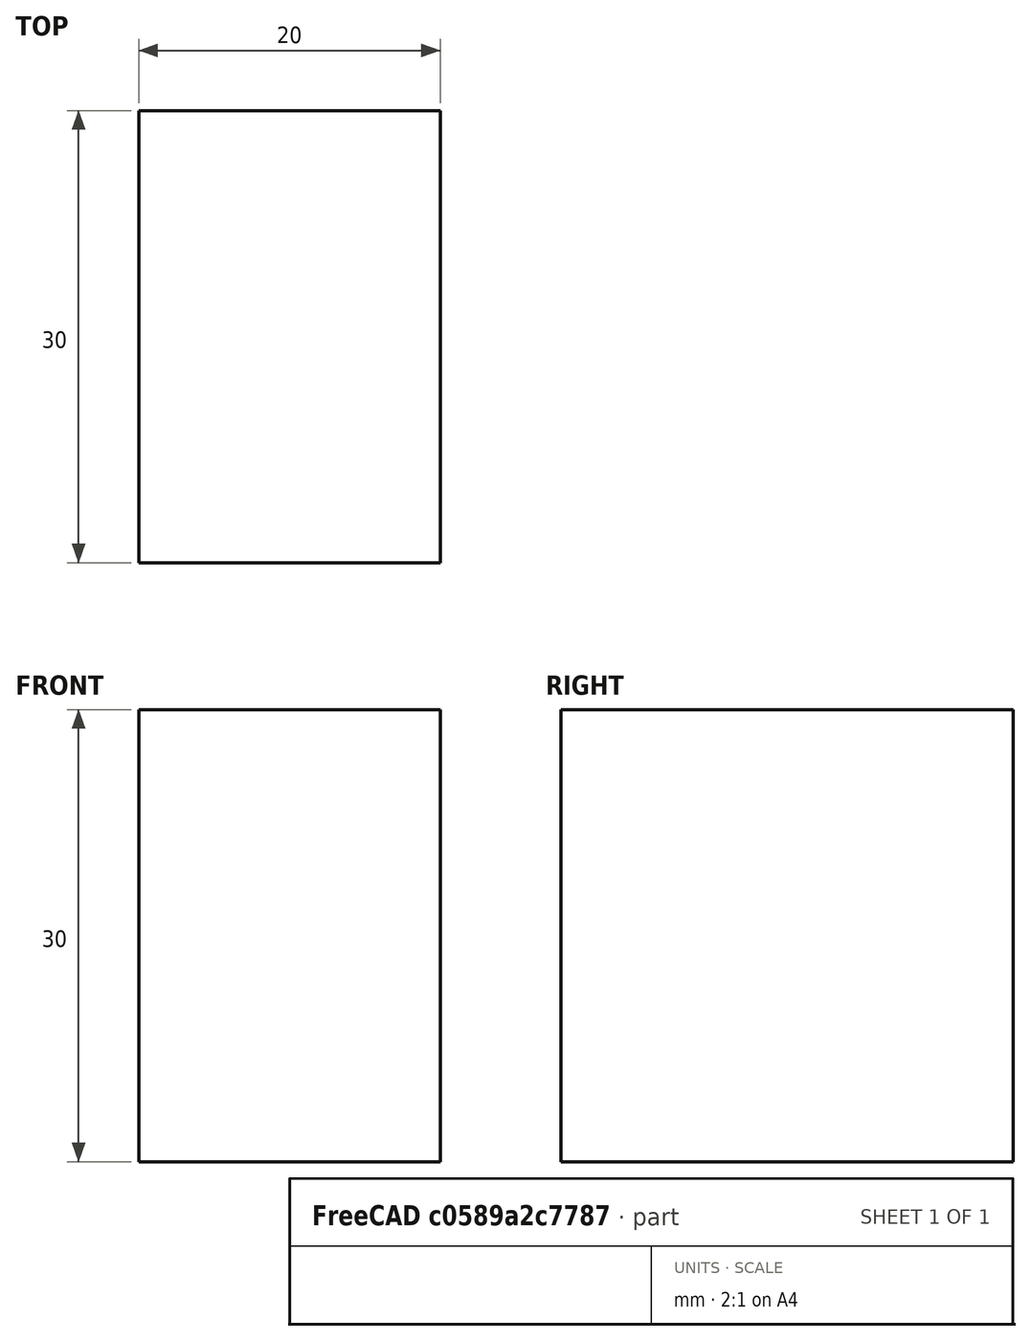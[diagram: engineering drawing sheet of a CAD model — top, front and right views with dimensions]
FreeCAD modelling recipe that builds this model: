
FCSTD DOCUMENT  (FreeCAD 1.1R20260325 (Git shallow))
Label: Tomada_personalizada
License: All rights reserved
LicenseURL: https://en.wikipedia.org/wiki/All_rights_reserved
objects: App::DocumentObjectGroup×7, Sketcher::SketchObject×1, Part::Box×1
note: 3 computed .brp shape members not serialized (recipe doc carries the construction recipe); baked Part::Feature solids carry a one-line shape summary decoded from their .brp

FEATURE [App::DocumentObjectGroup] Simbolo_2D
FEATURE [App::DocumentObjectGroup] Foto
FEATURE [App::DocumentObjectGroup] Modelo_3D
FEATURE [App::DocumentObjectGroup] Descricao
FEATURE [App::DocumentObjectGroup] Detalhes_2D
FEATURE [Sketcher::SketchObject] Tomada
  ArcFitTolerance = 1e-06
  Circuito = 1
  Descricao = Descrição da tomada
  ExternalTypes = [0]
  Fase = 2
  Fator_potencia = 0.9
  FullyConstrained = false
  MakeInternals = false
  Tensao = 220
  _ExternalGeoVersion = 1
  altura_piso = 30
  neutro = true
  potencia = 100
  terra = true
  tipo = tomada
  sketch-geometry (4):
    g0: LineSegment StartX=0 StartY=0 StartZ=0 EndX=33.3333 EndY=0 EndZ=0
    g1: LineSegment StartX=33.3333 StartY=25 StartZ=0 EndX=33.3333 EndY=-25 EndZ=0
    g2: LineSegment StartX=33.3333 StartY=25 StartZ=0 EndX=100 EndY=-3.6e-15 EndZ=0
    g3: LineSegment StartX=33.3333 StartY=-25 StartZ=0 EndX=100 EndY=3.6e-15 EndZ=0
FEATURE [App::DocumentObjectGroup] Tomadas
  Group = -> [Tomada]
FEATURE [Part::Box] tomada
  AttacherType = Attacher::AttachEngine3D
  Height = 30
  Length = 20
  Placement = pos=(-15,-10,30) rot=(0,0,1;0rad)
  Width = 30
FEATURE [App::DocumentObjectGroup] Equipamentos
  Group = -> [tomada]
